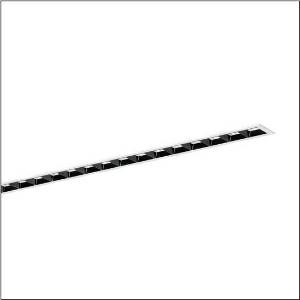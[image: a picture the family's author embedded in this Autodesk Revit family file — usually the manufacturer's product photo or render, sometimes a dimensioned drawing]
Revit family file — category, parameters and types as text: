
# Revit family: silica_r__21_51mx12da34wb_5af2
name_source: partatom
category: Lighting Fixtures
units: mm (PartAtom-declared; Revit-internal decimal feet)

## family parameters
Cut with Voids When Loaded = No
Host = Face
Light Source = No
Part Type = Normal
Room Calculation Point = No
Round Connector Dimension = Use Diameter
Shared = No

## types (1)
- --- (1 x LED, 4320 lm, 27.4 W, 3000K)
    Apparent Load = 27 VA
    CIE Flux Codes = 86 100 100 100 100
    Color Rendering = 80
    Color Temperature = 3000K
    Default Elevation = 1800 mm
    Description = Silica® 21, office luminaire, primary light control with darklight reflector, of PMMA, black, CAT 2 (L<= 3000cd/m²), light emission: direct distribution, primary light characteristic: symmetric, installation type: recessed, LED, rated luminous flux: 4.320lm, luminous efficacy: 158lm/W, light colour: 830, colour temperature: 3000K, control gear: DALI 2, with terminal, 3+2-pole, max. 2.5mm², mains connection: 220..240V, AC, 50/60Hz, rated input power: 27.4W, luminaire housing, of aluminium, traffic white (RAL 9016), length: 1.228mm, width: 79mm, height: 53mm, protection rating (complete): IP20, insulation class (complete): insulation class I (protective earthing), certification: CE, ENEC, VDE, permissible operating ambient temperature: 0..+35°C, standard: EN 50419, packaging unit: 1 piece
    Height = 0 mm  [stored 0 ft]
    Lamp = 1 x LED
    Lamp Light Flux = 4320 lm
    Lamp Power = 27.4 W
    Lamp count = 1
    Length = 1227 mm
    Luminous efficacy = 158 lm/W
    Manufacturer = Siteco
    ModVariant = No
    Model = 51MX12DA34WB
    Mounting Place = Ceiling
    Mounting Type = Recessed
    Number of Poles = 1
    OnlyDefault = Yes
    Power Factor = 1
    Product Name = Silica® 21
    Product group = office luminaire | ceiling recessed
    ProductGroupID = 401
    Protection Class = Protection class I
    Protection Degree = IP 20
    RLX_Detail_Level = 1
    RLX_Emergency_Light_Flux = 0 lm
    RLX_Emergency_Type = 0
    RLX_Emergency_Type_DB = No
    RlxData = <blob elided: 38977 chars, md5=2f79bcbb>
    Socket = socket
    Standby Power = 0 W
    System Light Flux = 4320 lm
    System Power = 27 W
    Type Comments = factory setting: luminous flux: 100 % | dim-lin: 254 | 392 mA
    Type Image = l_1335880.jpg
    URL = http://relux.com
    VarID = @adj_008583
    Voltage = 0 V
    Weight = 0.00 kg
    Width = 79 mm

note: [stored X ft] marks values corroborated as IEEE doubles in the binary element streams (Revit-internal decimal feet)

## geometry (parser evidence)
native form markers: Blend x4, Sweep x10
no freeform markers — native parametric forms only
